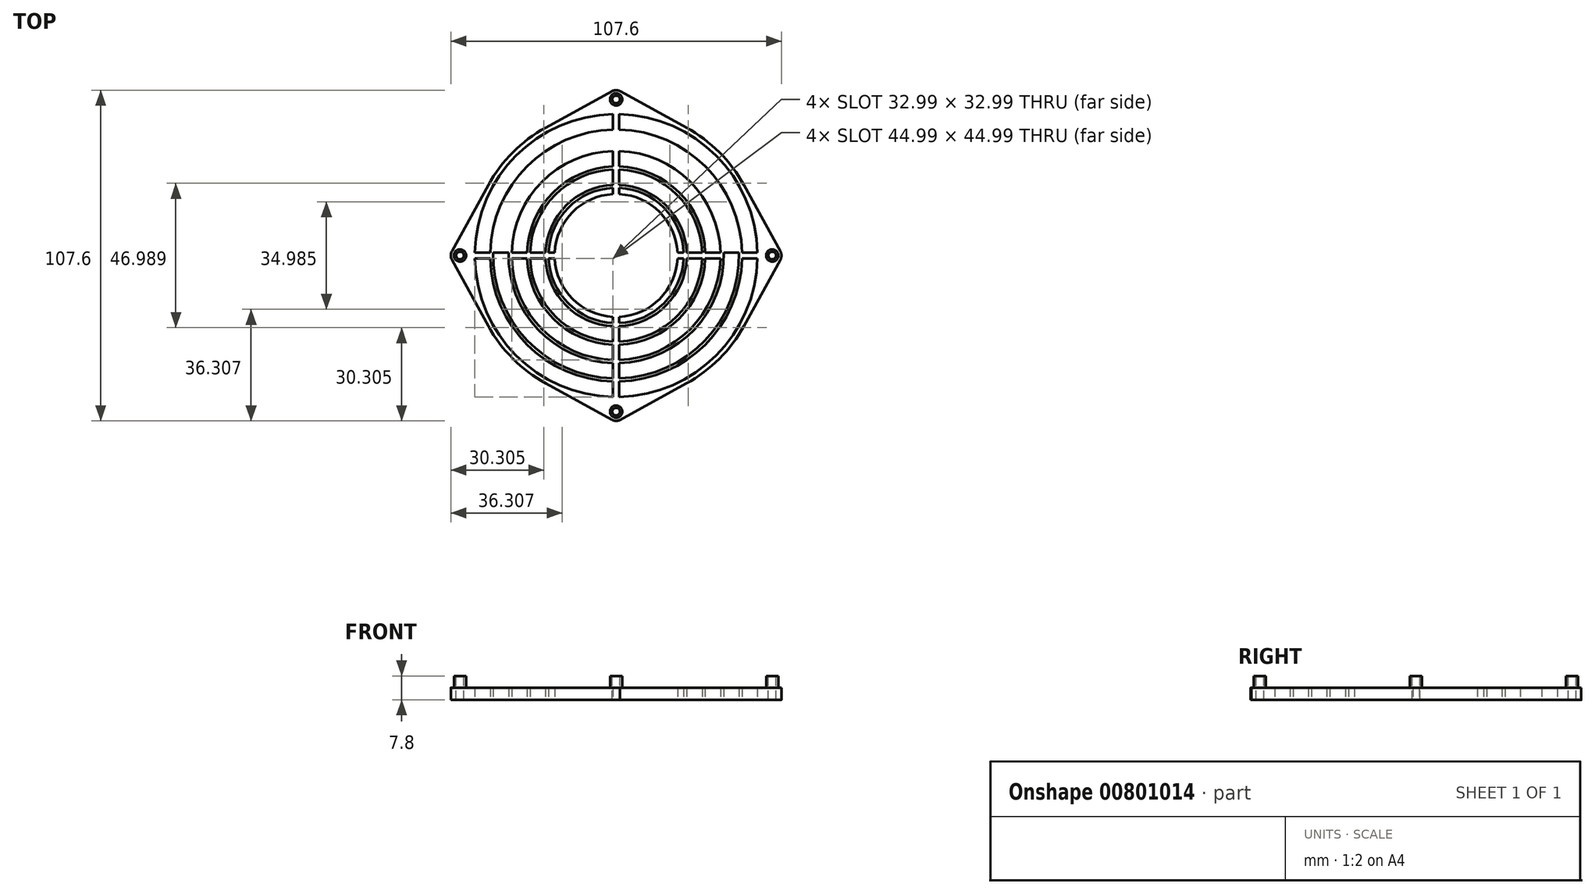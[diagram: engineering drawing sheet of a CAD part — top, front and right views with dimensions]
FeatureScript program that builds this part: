
annotation { "Feature Type Name" : "Feature", "Feature Type Description" : "" }
export const myFeature = defineFeature(function(context is Context, id is Id, definition is map)
    precondition{}
    {
        {
            var Q0;
            Q0=qCreatedBy(makeId("Top.planeOp"),FACE);
            var sketch = newSketch(context, id + "F0", { "sketchPlane" : qUnion([Q0])});
            skCircle(sketch, "E0", {"center": v(0, 0) * mm, "radius": 47.5 * mm});
            skCircle(sketch, "E1", {"center": v(0, 0) * mm, "radius": 46 * mm});
            skCircle(sketch, "E2", {"center": v(0, 0) * mm, "radius": 41 * mm});
            skCircle(sketch, "E3", {"center": v(0, 0) * mm, "radius": 40 * mm});
            skCircle(sketch, "E4", {"center": v(0, 0) * mm, "radius": 35 * mm});
            skCircle(sketch, "E5", {"center": v(0, 0) * mm, "radius": 34 * mm});
            skCircle(sketch, "E6", {"center": v(0, 0) * mm, "radius": 29 * mm});
            skCircle(sketch, "E7", {"center": v(0, 0) * mm, "radius": 28 * mm});
            skCircle(sketch, "E8", {"center": v(0, 0) * mm, "radius": 23 * mm});
            skCircle(sketch, "E9", {"center": v(0, 0) * mm, "radius": 22 * mm});
            skCircle(sketch, "E10", {"center": v(0, 0) * mm, "radius": 20 * mm});
            skLineSegment(sketch, "E11.bottom", {"start": v(-1, 47.49) * mm, "end": v(1, 47.49) * mm});
            skLineSegment(sketch, "E11.top", {"start": v(-1, -47.49) * mm, "end": v(1, -47.49) * mm});
            skLineSegment(sketch, "E11.left", {"start": v(-1, 47.49) * mm, "end": v(-1, -47.49) * mm});
            skLineSegment(sketch, "E11.right", {"start": v(1, 47.49) * mm, "end": v(1, -47.49) * mm});
            skLineSegment(sketch, "E12.bottom", {"start": v(-47.49, 1) * mm, "end": v(47.49, 1) * mm});
            skLineSegment(sketch, "E12.top", {"start": v(-47.49, -1) * mm, "end": v(47.49, -1) * mm});
            skLineSegment(sketch, "E12.left", {"start": v(-47.49, 1) * mm, "end": v(-47.49, -1) * mm});
            skLineSegment(sketch, "E12.right", {"start": v(47.49, 1) * mm, "end": v(47.49, -1) * mm});
            skCircle(sketch, "E13", {"center": v(0, 0) * mm, "radius": 50.8 * mm});
            skLineSegment(sketch, "E14", {"start": v(0, 64.35) * mm, "end": v(0, -68.55) * mm, "construction": true});
            skLineSegment(sketch, "E15", {"start": v(-68.61, 0) * mm, "end": v(59.97, 0) * mm, "construction": true});
            skCircle(sketch, "E16", {"center": v(0, 50.8) * mm, "radius": 2 * mm});
            skCircle(sketch, "E17", {"center": v(50.8, 0) * mm, "radius": 2 * mm});
            skCircle(sketch, "E18", {"center": v(0, -50.8) * mm, "radius": 2 * mm});
            skCircle(sketch, "E19", {"center": v(-50.8, 0) * mm, "radius": 2 * mm});
            skCircle(sketch, "E20", {"center": v(0, 50.8) * mm, "radius": 3 * mm});
            skLineSegment(sketch, "E21", {"start": v(-22.91, 41.6) * mm, "end": v(-1.45, 53.43) * mm});
            skCircle(sketch, "E22", {"center": v(-50.8, 0) * mm, "radius": 3 * mm});
            skCircle(sketch, "E23", {"center": v(0, -50.8) * mm, "radius": 3 * mm});
            skCircle(sketch, "E24", {"center": v(50.8, 0) * mm, "radius": 3 * mm});
            skLineSegment(sketch, "E25", {"start": v(53.43, -1.45) * mm, "end": v(41.6, -22.91) * mm});
            skLineSegment(sketch, "E26", {"start": v(53.43, 1.45) * mm, "end": v(41.6, 22.91) * mm});
            skLineSegment(sketch, "E27", {"start": v(1.45, 53.43) * mm, "end": v(22.91, 41.6) * mm});
            skLineSegment(sketch, "E28", {"start": v(-1.45, -53.43) * mm, "end": v(-22.91, -41.6) * mm});
            skLineSegment(sketch, "E29", {"start": v(1.2, -53.55) * mm, "end": v(22.89, -41.62) * mm});
            skLineSegment(sketch, "E30", {"start": v(-53.43, -1.45) * mm, "end": v(-41.6, -22.91) * mm});
            skLineSegment(sketch, "E31", {"start": v(-53.43, 1.45) * mm, "end": v(-41.6, 22.91) * mm});
            skSolve(sketch);
        }
        {
            var Q0;
            {var subQ0=sQuery(id+"F0.wireOp",EDGE,"E12.bottom");var subQ1=sQuery(id+"F0.wireOp",EDGE,"E6");var subQ2=makeQuery(id+"F0.imprint","INTERSECT",VERTEX,{"disambiguationData":[OD(1.0)],"derivedFrom":[subQ1,subQ0]});Q0=makeQuery(id+"F0.imprint","IMPRINT",FACE,{"disambiguationData":[TD([[makeQuery(id+"F0.imprint","IMPRINT",EDGE,{"disambiguationData":[TD([[subQ2,-1.0]])],"derivedFrom":subQ1}),1.0]])]});}
            var Q1;
            {var subQ1=sQuery(id+"F0.wireOp",EDGE,"E0");var subQ8=makeQuery(id+"F0.imprint","INTERSECT",VERTEX,{"derivedFrom":[subQ1,sQuery(id+"F0.wireOp",EDGE,"E26")]});Q1=makeQuery(id+"F0.imprint","IMPRINT",FACE,{"disambiguationData":[TD([[makeQuery(id+"F0.imprint","IMPRINT",EDGE,{"disambiguationData":[TD([[subQ8,-1.0]])],"derivedFrom":subQ1}),1.0]])]});}
            var Q2;
            {var subQ0=sQuery(id+"F0.wireOp",EDGE,"E11.right");var subQ1=sQuery(id+"F0.wireOp",EDGE,"E9");var subQ2=makeQuery(id+"F0.imprint","INTERSECT",VERTEX,{"disambiguationData":[OD(0.0)],"derivedFrom":[subQ1,subQ0]});Q2=makeQuery(id+"F0.imprint","IMPRINT",FACE,{"disambiguationData":[TD([[makeQuery(id+"F0.imprint","IMPRINT",EDGE,{"disambiguationData":[TD([[subQ2,-1.0]])],"derivedFrom":subQ1}),1.0]])]});}
            var Q3;
            {var subQ0=sQuery(id+"F0.wireOp",EDGE,"E12.bottom");var subQ1=sQuery(id+"F0.wireOp",EDGE,"E5");var subQ2=makeQuery(id+"F0.imprint","INTERSECT",VERTEX,{"disambiguationData":[OD(1.0)],"derivedFrom":[subQ1,subQ0]});Q3=makeQuery(id+"F0.imprint","IMPRINT",FACE,{"disambiguationData":[TD([[makeQuery(id+"F0.imprint","IMPRINT",EDGE,{"disambiguationData":[TD([[subQ2,-1.0]])],"derivedFrom":subQ1}),1.0]])]});}
            var Q4;
            {var subQ0=sQuery(id+"F0.wireOp",EDGE,"E28");var subQ1=sQuery(id+"F0.wireOp",EDGE,"E13");var subQ2=makeQuery(id+"F0.imprint","INTERSECT",VERTEX,{"derivedFrom":[subQ1,subQ0]});Q4=makeQuery(id+"F0.imprint","IMPRINT",FACE,{"disambiguationData":[TD([[makeQuery(id+"F0.imprint","IMPRINT",EDGE,{"disambiguationData":[TD([[subQ2,-1.0]])],"derivedFrom":subQ1}),1.0]])]});}
            var Q5;
            {var subQ0=sQuery(id+"F0.wireOp",EDGE,"E11.right");var subQ1=sQuery(id+"F0.wireOp",EDGE,"E10");var subQ2=makeQuery(id+"F0.imprint","INTERSECT",VERTEX,{"disambiguationData":[OD(0.0)],"derivedFrom":[subQ1,subQ0]});Q5=makeQuery(id+"F0.imprint","IMPRINT",FACE,{"disambiguationData":[TD([[makeQuery(id+"F0.imprint","IMPRINT",EDGE,{"disambiguationData":[TD([[subQ2,1.0]])],"derivedFrom":subQ1}),1.0]])]});}
            var Q6;
            {var subQ0=sQuery(id+"F0.wireOp",EDGE,"E11.right");var subQ1=sQuery(id+"F0.wireOp",EDGE,"E7");var subQ2=makeQuery(id+"F0.imprint","INTERSECT",VERTEX,{"disambiguationData":[OD(0.0)],"derivedFrom":[subQ1,subQ0]});Q6=makeQuery(id+"F0.imprint","IMPRINT",FACE,{"disambiguationData":[TD([[makeQuery(id+"F0.imprint","IMPRINT",EDGE,{"disambiguationData":[TD([[subQ2,-1.0]])],"derivedFrom":subQ1}),1.0]])]});}
            var Q7;
            {var subQ0=sQuery(id+"F0.wireOp",EDGE,"E11.right");var subQ1=sQuery(id+"F0.wireOp",EDGE,"E5");var subQ2=makeQuery(id+"F0.imprint","INTERSECT",VERTEX,{"disambiguationData":[OD(0.0)],"derivedFrom":[subQ1,subQ0]});Q7=makeQuery(id+"F0.imprint","IMPRINT",FACE,{"disambiguationData":[TD([[makeQuery(id+"F0.imprint","IMPRINT",EDGE,{"disambiguationData":[TD([[subQ2,-1.0]])],"derivedFrom":subQ1}),1.0]])]});}
            var Q8;
            {var subQ0=sQuery(id+"F0.wireOp",EDGE,"E12.bottom");var subQ1=sQuery(id+"F0.wireOp",EDGE,"E7");var subQ2=makeQuery(id+"F0.imprint","INTERSECT",VERTEX,{"disambiguationData":[OD(0.0)],"derivedFrom":[subQ1,subQ0]});Q8=makeQuery(id+"F0.imprint","IMPRINT",FACE,{"disambiguationData":[TD([[makeQuery(id+"F0.imprint","IMPRINT",EDGE,{"disambiguationData":[TD([[subQ2,1.0]])],"derivedFrom":subQ1}),1.0]])]});}
            var Q9;
            {var subQ0=sQuery(id+"F0.wireOp",EDGE,"E12.bottom");var subQ1=sQuery(id+"F0.wireOp",EDGE,"E5");var subQ2=makeQuery(id+"F0.imprint","INTERSECT",VERTEX,{"disambiguationData":[OD(0.0)],"derivedFrom":[subQ1,subQ0]});Q9=makeQuery(id+"F0.imprint","IMPRINT",FACE,{"disambiguationData":[TD([[makeQuery(id+"F0.imprint","IMPRINT",EDGE,{"disambiguationData":[TD([[subQ2,1.0]])],"derivedFrom":subQ1}),1.0]])]});}
            var Q10;
            {var subQ1=sQuery(id+"F0.wireOp",EDGE,"E0");var subQ3=makeQuery(id+"F0.imprint","INTERSECT",VERTEX,{"derivedFrom":[subQ1,sQuery(id+"F0.wireOp",EDGE,"E25")]});Q10=makeQuery(id+"F0.imprint","IMPRINT",FACE,{"disambiguationData":[TD([[makeQuery(id+"F0.imprint","IMPRINT",EDGE,{"disambiguationData":[TD([[subQ3,1.0]])],"derivedFrom":subQ1}),1.0]])]});}
            var Q11;
            {var subQ0=sQuery(id+"F0.wireOp",EDGE,"E12.bottom");var subQ1=sQuery(id+"F0.wireOp",EDGE,"E3");var subQ2=makeQuery(id+"F0.imprint","INTERSECT",VERTEX,{"disambiguationData":[OD(0.0)],"derivedFrom":[subQ1,subQ0]});Q11=makeQuery(id+"F0.imprint","IMPRINT",FACE,{"disambiguationData":[TD([[makeQuery(id+"F0.imprint","IMPRINT",EDGE,{"disambiguationData":[TD([[subQ2,1.0]])],"derivedFrom":subQ1}),1.0]])]});}
            var Q12;
            {var subQ0=sQuery(id+"F0.wireOp",EDGE,"E20");var subQ4=sQuery(id+"F0.wireOp",EDGE,"E13");var subQ8=makeQuery(id+"F0.imprint","INTERSECT",VERTEX,{"disambiguationData":[OD(0.0)],"derivedFrom":[subQ4,subQ0]});Q12=makeQuery(id+"F0.imprint","IMPRINT",FACE,{"disambiguationData":[TD([[makeQuery(id+"F0.imprint","IMPRINT",EDGE,{"disambiguationData":[TD([[subQ8,-1.0]])],"derivedFrom":subQ4}),-1.0]])]});}
            var Q13;
            {var subQ0=sQuery(id+"F0.wireOp",EDGE,"E11.right");var subQ1=sQuery(id+"F0.wireOp",EDGE,"E3");var subQ2=makeQuery(id+"F0.imprint","INTERSECT",VERTEX,{"disambiguationData":[OD(0.0)],"derivedFrom":[subQ1,subQ0]});Q13=makeQuery(id+"F0.imprint","IMPRINT",FACE,{"disambiguationData":[TD([[makeQuery(id+"F0.imprint","IMPRINT",EDGE,{"disambiguationData":[TD([[subQ2,-1.0]])],"derivedFrom":subQ1}),1.0]])]});}
            var Q14;
            {var subQ0=sQuery(id+"F0.wireOp",EDGE,"E24");var subQ1=sQuery(id+"F0.wireOp",EDGE,"E13");var subQ2=makeQuery(id+"F0.imprint","INTERSECT",VERTEX,{"disambiguationData":[OD(0.0)],"derivedFrom":[subQ1,subQ0]});Q14=makeQuery(id+"F0.imprint","IMPRINT",FACE,{"disambiguationData":[TD([[makeQuery(id+"F0.imprint","IMPRINT",EDGE,{"disambiguationData":[TD([[subQ2,1.0]])],"derivedFrom":subQ1}),1.0]])]});}
            var Q15;
            {var subQ0=sQuery(id+"F0.wireOp",EDGE,"E11.right");var subQ1=sQuery(id+"F0.wireOp",EDGE,"E6");var subQ2=makeQuery(id+"F0.imprint","INTERSECT",VERTEX,{"disambiguationData":[OD(0.0)],"derivedFrom":[subQ1,subQ0]});Q15=makeQuery(id+"F0.imprint","IMPRINT",FACE,{"disambiguationData":[TD([[makeQuery(id+"F0.imprint","IMPRINT",EDGE,{"disambiguationData":[TD([[subQ2,-1.0]])],"derivedFrom":subQ1}),1.0]])]});}
            var Q16;
            {var subQ0=sQuery(id+"F0.wireOp",EDGE,"E18");var subQ1=sQuery(id+"F0.wireOp",EDGE,"E13");var subQ2=makeQuery(id+"F0.imprint","INTERSECT",VERTEX,{"disambiguationData":[OD(0.0)],"derivedFrom":[subQ1,subQ0]});Q16=makeQuery(id+"F0.imprint","IMPRINT",FACE,{"disambiguationData":[TD([[makeQuery(id+"F0.imprint","IMPRINT",EDGE,{"disambiguationData":[TD([[subQ2,-1.0]])],"derivedFrom":subQ1}),1.0]])]});}
            var Q17;
            {var subQ5=sQuery(id+"F0.wireOp",EDGE,"E0");var subQ8=makeQuery(id+"F0.imprint","INTERSECT",VERTEX,{"derivedFrom":[subQ5,sQuery(id+"F0.wireOp",EDGE,"E21")]});Q17=makeQuery(id+"F0.imprint","IMPRINT",FACE,{"disambiguationData":[TD([[makeQuery(id+"F0.imprint","IMPRINT",EDGE,{"disambiguationData":[TD([[subQ8,-1.0]])],"derivedFrom":subQ5}),1.0]])]});}
            var Q18;
            {var subQ0=sQuery(id+"F0.wireOp",EDGE,"E18");var subQ1=sQuery(id+"F0.wireOp",EDGE,"E13");var subQ2=makeQuery(id+"F0.imprint","INTERSECT",VERTEX,{"disambiguationData":[OD(0.0)],"derivedFrom":[subQ1,subQ0]});Q18=makeQuery(id+"F0.imprint","IMPRINT",FACE,{"disambiguationData":[TD([[makeQuery(id+"F0.imprint","IMPRINT",EDGE,{"disambiguationData":[TD([[subQ2,-1.0]])],"derivedFrom":subQ1}),-1.0]])]});}
            var Q19;
            {var subQ6=sQuery(id+"F0.wireOp",EDGE,"E13");var subQ10=sQuery(id+"F0.wireOp",EDGE,"E31");var subQ11=makeQuery(id+"F0.imprint","INTERSECT",VERTEX,{"derivedFrom":[subQ6,subQ10]});Q19=makeQuery(id+"F0.imprint","IMPRINT",FACE,{"disambiguationData":[TD([[makeQuery(id+"F0.imprint","IMPRINT",EDGE,{"disambiguationData":[TD([[subQ11,-1.0]])],"derivedFrom":subQ6}),1.0]])]});}
            var Q20;
            {var subQ1=sQuery(id+"F0.wireOp",EDGE,"E13");var subQ4=sQuery(id+"F0.wireOp",EDGE,"E23");var subQ7=makeQuery(id+"F0.imprint","INTERSECT",VERTEX,{"disambiguationData":[OD(0.0)],"derivedFrom":[subQ1,subQ4]});Q20=makeQuery(id+"F0.imprint","IMPRINT",FACE,{"disambiguationData":[TD([[makeQuery(id+"F0.imprint","IMPRINT",EDGE,{"disambiguationData":[TD([[subQ7,-1.0]])],"derivedFrom":subQ1}),-1.0]])]});}
            var Q21;
            {var subQ0=sQuery(id+"F0.wireOp",EDGE,"E12.bottom");var subQ1=sQuery(id+"F0.wireOp",EDGE,"E4");var subQ2=makeQuery(id+"F0.imprint","INTERSECT",VERTEX,{"disambiguationData":[OD(1.0)],"derivedFrom":[subQ1,subQ0]});Q21=makeQuery(id+"F0.imprint","IMPRINT",FACE,{"disambiguationData":[TD([[makeQuery(id+"F0.imprint","IMPRINT",EDGE,{"disambiguationData":[TD([[subQ2,-1.0]])],"derivedFrom":subQ1}),1.0]])]});}
            var Q22;
            {var subQ0=sQuery(id+"F0.wireOp",EDGE,"E22");var subQ1=sQuery(id+"F0.wireOp",EDGE,"E13");var subQ2=makeQuery(id+"F0.imprint","INTERSECT",VERTEX,{"disambiguationData":[OD(0.0)],"derivedFrom":[subQ1,subQ0]});Q22=makeQuery(id+"F0.imprint","IMPRINT",FACE,{"disambiguationData":[TD([[makeQuery(id+"F0.imprint","IMPRINT",EDGE,{"disambiguationData":[TD([[subQ2,-1.0]])],"derivedFrom":subQ1}),1.0]])]});}
            var Q23;
            {var subQ0=sQuery(id+"F0.wireOp",EDGE,"E11.right");var subQ1=sQuery(id+"F0.wireOp",EDGE,"E8");var subQ2=makeQuery(id+"F0.imprint","INTERSECT",VERTEX,{"disambiguationData":[OD(0.0)],"derivedFrom":[subQ1,subQ0]});Q23=makeQuery(id+"F0.imprint","IMPRINT",FACE,{"disambiguationData":[TD([[makeQuery(id+"F0.imprint","IMPRINT",EDGE,{"disambiguationData":[TD([[subQ2,1.0]])],"derivedFrom":subQ1}),1.0]])]});}
            var Q24;
            {var subQ0=sQuery(id+"F0.wireOp",EDGE,"E29");var subQ1=sQuery(id+"F0.wireOp",EDGE,"E13");var subQ2=makeQuery(id+"F0.imprint","INTERSECT",VERTEX,{"derivedFrom":[subQ1,subQ0]});Q24=makeQuery(id+"F0.imprint","IMPRINT",FACE,{"disambiguationData":[TD([[makeQuery(id+"F0.imprint","IMPRINT",EDGE,{"disambiguationData":[TD([[subQ2,1.0]])],"derivedFrom":subQ1}),-1.0]])]});}
            var Q25;
            {var subQ0=sQuery(id+"F0.wireOp",EDGE,"E31");var subQ1=sQuery(id+"F0.wireOp",EDGE,"E13");var subQ2=makeQuery(id+"F0.imprint","INTERSECT",VERTEX,{"derivedFrom":[subQ1,subQ0]});Q25=makeQuery(id+"F0.imprint","IMPRINT",FACE,{"disambiguationData":[TD([[makeQuery(id+"F0.imprint","IMPRINT",EDGE,{"disambiguationData":[TD([[subQ2,-1.0]])],"derivedFrom":subQ1}),-1.0]])]});}
            var Q26;
            {var subQ0=sQuery(id+"F0.wireOp",EDGE,"E12.bottom");var subQ1=sQuery(id+"F0.wireOp",EDGE,"E10");var subQ2=makeQuery(id+"F0.imprint","INTERSECT",VERTEX,{"disambiguationData":[OD(0.0)],"derivedFrom":[subQ1,subQ0]});Q26=makeQuery(id+"F0.imprint","IMPRINT",FACE,{"disambiguationData":[TD([[makeQuery(id+"F0.imprint","IMPRINT",EDGE,{"disambiguationData":[TD([[subQ2,1.0]])],"derivedFrom":subQ1}),1.0]])]});}
            var Q27;
            {var subQ0=sQuery(id+"F0.wireOp",EDGE,"E11.right");var subQ1=sQuery(id+"F0.wireOp",EDGE,"E8");var subQ2=makeQuery(id+"F0.imprint","INTERSECT",VERTEX,{"disambiguationData":[OD(0.0)],"derivedFrom":[subQ1,subQ0]});Q27=makeQuery(id+"F0.imprint","IMPRINT",FACE,{"disambiguationData":[TD([[makeQuery(id+"F0.imprint","IMPRINT",EDGE,{"disambiguationData":[TD([[subQ2,-1.0]])],"derivedFrom":subQ1}),1.0]])]});}
            var Q28;
            {var subQ0=sQuery(id+"F0.wireOp",EDGE,"E19");var subQ1=sQuery(id+"F0.wireOp",EDGE,"E13");var subQ2=makeQuery(id+"F0.imprint","INTERSECT",VERTEX,{"disambiguationData":[OD(0.0)],"derivedFrom":[subQ1,subQ0]});Q28=makeQuery(id+"F0.imprint","IMPRINT",FACE,{"disambiguationData":[TD([[makeQuery(id+"F0.imprint","IMPRINT",EDGE,{"disambiguationData":[TD([[subQ2,-1.0]])],"derivedFrom":subQ1}),-1.0]])]});}
            var Q29;
            {var subQ0=sQuery(id+"F0.wireOp",EDGE,"E27");var subQ1=sQuery(id+"F0.wireOp",EDGE,"E13");var subQ2=makeQuery(id+"F0.imprint","INTERSECT",VERTEX,{"derivedFrom":[subQ1,subQ0]});Q29=makeQuery(id+"F0.imprint","IMPRINT",FACE,{"disambiguationData":[TD([[makeQuery(id+"F0.imprint","IMPRINT",EDGE,{"disambiguationData":[TD([[subQ2,-1.0]])],"derivedFrom":subQ1}),-1.0]])]});}
            var Q30;
            {var subQ0=sQuery(id+"F0.wireOp",EDGE,"E12.bottom");var subQ1=sQuery(id+"F0.wireOp",EDGE,"E3");var subQ2=makeQuery(id+"F0.imprint","INTERSECT",VERTEX,{"disambiguationData":[OD(1.0)],"derivedFrom":[subQ1,subQ0]});Q30=makeQuery(id+"F0.imprint","IMPRINT",FACE,{"disambiguationData":[TD([[makeQuery(id+"F0.imprint","IMPRINT",EDGE,{"disambiguationData":[TD([[subQ2,-1.0]])],"derivedFrom":subQ1}),1.0]])]});}
            var Q31;
            {var subQ0=sQuery(id+"F0.wireOp",EDGE,"E20");var subQ1=sQuery(id+"F0.wireOp",EDGE,"E13");var subQ2=makeQuery(id+"F0.imprint","INTERSECT",VERTEX,{"disambiguationData":[OD(0.0)],"derivedFrom":[subQ1,subQ0]});Q31=makeQuery(id+"F0.imprint","IMPRINT",FACE,{"disambiguationData":[TD([[makeQuery(id+"F0.imprint","IMPRINT",EDGE,{"disambiguationData":[TD([[subQ2,-1.0]])],"derivedFrom":subQ1}),1.0]])]});}
            var Q32;
            {var subQ5=sQuery(id+"F0.wireOp",EDGE,"E0");var subQ6=makeQuery(id+"F0.imprint","INTERSECT",VERTEX,{"derivedFrom":[subQ5,sQuery(id+"F0.wireOp",EDGE,"E28")]});Q32=makeQuery(id+"F0.imprint","IMPRINT",FACE,{"disambiguationData":[TD([[makeQuery(id+"F0.imprint","IMPRINT",EDGE,{"disambiguationData":[TD([[subQ6,1.0]])],"derivedFrom":subQ5}),1.0]])]});}
            var Q33;
            {var subQ0=sQuery(id+"F0.wireOp",EDGE,"E17");var subQ1=sQuery(id+"F0.wireOp",EDGE,"E13");var subQ2=makeQuery(id+"F0.imprint","INTERSECT",VERTEX,{"disambiguationData":[OD(0.0)],"derivedFrom":[subQ1,subQ0]});Q33=makeQuery(id+"F0.imprint","IMPRINT",FACE,{"disambiguationData":[TD([[makeQuery(id+"F0.imprint","IMPRINT",EDGE,{"disambiguationData":[TD([[subQ2,1.0]])],"derivedFrom":subQ1}),1.0]])]});}
            var Q34;
            {var subQ0=sQuery(id+"F0.wireOp",EDGE,"E26");var subQ1=sQuery(id+"F0.wireOp",EDGE,"E13");var subQ2=makeQuery(id+"F0.imprint","INTERSECT",VERTEX,{"derivedFrom":[subQ1,subQ0]});Q34=makeQuery(id+"F0.imprint","IMPRINT",FACE,{"disambiguationData":[TD([[makeQuery(id+"F0.imprint","IMPRINT",EDGE,{"disambiguationData":[TD([[subQ2,1.0]])],"derivedFrom":subQ1}),-1.0]])]});}
            var Q35;
            {var subQ0=sQuery(id+"F0.wireOp",EDGE,"E26");var subQ1=sQuery(id+"F0.wireOp",EDGE,"E13");var subQ2=makeQuery(id+"F0.imprint","INTERSECT",VERTEX,{"derivedFrom":[subQ1,subQ0]});Q35=makeQuery(id+"F0.imprint","IMPRINT",FACE,{"disambiguationData":[TD([[makeQuery(id+"F0.imprint","IMPRINT",EDGE,{"disambiguationData":[TD([[subQ2,1.0]])],"derivedFrom":subQ1}),1.0]])]});}
            var Q36;
            {var subQ0=sQuery(id+"F0.wireOp",EDGE,"E11.right");var subQ1=sQuery(id+"F0.wireOp",EDGE,"E2");var subQ2=makeQuery(id+"F0.imprint","INTERSECT",VERTEX,{"disambiguationData":[OD(0.0)],"derivedFrom":[subQ1,subQ0]});Q36=makeQuery(id+"F0.imprint","IMPRINT",FACE,{"disambiguationData":[TD([[makeQuery(id+"F0.imprint","IMPRINT",EDGE,{"disambiguationData":[TD([[subQ2,-1.0]])],"derivedFrom":subQ1}),1.0]])]});}
            var Q37;
            {var subQ0=sQuery(id+"F0.wireOp",EDGE,"E16");var subQ1=sQuery(id+"F0.wireOp",EDGE,"E13");var subQ2=makeQuery(id+"F0.imprint","INTERSECT",VERTEX,{"disambiguationData":[OD(0.0)],"derivedFrom":[subQ1,subQ0]});Q37=makeQuery(id+"F0.imprint","IMPRINT",FACE,{"disambiguationData":[TD([[makeQuery(id+"F0.imprint","IMPRINT",EDGE,{"disambiguationData":[TD([[subQ2,-1.0]])],"derivedFrom":subQ1}),1.0]])]});}
            var Q38;
            {var subQ0=sQuery(id+"F0.wireOp",EDGE,"E12.bottom");var subQ1=sQuery(id+"F0.wireOp",EDGE,"E1");var subQ2=makeQuery(id+"F0.imprint","INTERSECT",VERTEX,{"disambiguationData":[OD(1.0)],"derivedFrom":[subQ1,subQ0]});Q38=makeQuery(id+"F0.imprint","IMPRINT",FACE,{"disambiguationData":[TD([[makeQuery(id+"F0.imprint","IMPRINT",EDGE,{"disambiguationData":[TD([[subQ2,-1.0]])],"derivedFrom":subQ1}),1.0]])]});}
            var Q39;
            {var subQ0=sQuery(id+"F0.wireOp",EDGE,"E12.bottom");var subQ1=sQuery(id+"F0.wireOp",EDGE,"E7");var subQ2=makeQuery(id+"F0.imprint","INTERSECT",VERTEX,{"disambiguationData":[OD(1.0)],"derivedFrom":[subQ1,subQ0]});Q39=makeQuery(id+"F0.imprint","IMPRINT",FACE,{"disambiguationData":[TD([[makeQuery(id+"F0.imprint","IMPRINT",EDGE,{"disambiguationData":[TD([[subQ2,-1.0]])],"derivedFrom":subQ1}),1.0]])]});}
            var Q40;
            {var subQ0=sQuery(id+"F0.wireOp",EDGE,"E11.left");var subQ1=sQuery(id+"F0.wireOp",EDGE,"E1");var subQ2=makeQuery(id+"F0.imprint","INTERSECT",VERTEX,{"disambiguationData":[OD(1.0)],"derivedFrom":[subQ1,subQ0]});Q40=makeQuery(id+"F0.imprint","IMPRINT",FACE,{"disambiguationData":[TD([[makeQuery(id+"F0.imprint","IMPRINT",EDGE,{"disambiguationData":[TD([[subQ2,-1.0]])],"derivedFrom":subQ1}),1.0]])]});}
            var Q41;
            {var subQ0=sQuery(id+"F0.wireOp",EDGE,"E22");var subQ2=sQuery(id+"F0.wireOp",EDGE,"E13");var subQ3=makeQuery(id+"F0.imprint","INTERSECT",VERTEX,{"disambiguationData":[OD(0.0)],"derivedFrom":[subQ2,subQ0]});Q41=makeQuery(id+"F0.imprint","IMPRINT",FACE,{"disambiguationData":[TD([[makeQuery(id+"F0.imprint","IMPRINT",EDGE,{"disambiguationData":[TD([[subQ3,-1.0]])],"derivedFrom":subQ2}),-1.0]])]});}
            var Q42;
            {var subQ0=sQuery(id+"F0.wireOp",EDGE,"E27");var subQ1=sQuery(id+"F0.wireOp",EDGE,"E13");var subQ2=makeQuery(id+"F0.imprint","INTERSECT",VERTEX,{"derivedFrom":[subQ1,subQ0]});Q42=makeQuery(id+"F0.imprint","IMPRINT",FACE,{"disambiguationData":[TD([[makeQuery(id+"F0.imprint","IMPRINT",EDGE,{"disambiguationData":[TD([[subQ2,-1.0]])],"derivedFrom":subQ1}),1.0]])]});}
            var Q43;
            {var subQ0=sQuery(id+"F0.wireOp",EDGE,"E11.right");var subQ1=sQuery(id+"F0.wireOp",EDGE,"E1");var subQ2=makeQuery(id+"F0.imprint","INTERSECT",VERTEX,{"disambiguationData":[OD(0.0)],"derivedFrom":[subQ1,subQ0]});Q43=makeQuery(id+"F0.imprint","IMPRINT",FACE,{"disambiguationData":[TD([[makeQuery(id+"F0.imprint","IMPRINT",EDGE,{"disambiguationData":[TD([[subQ2,-1.0]])],"derivedFrom":subQ1}),1.0]])]});}
            var Q44;
            {var subQ0=sQuery(id+"F0.wireOp",EDGE,"E12.bottom");var subQ1=sQuery(id+"F0.wireOp",EDGE,"E4");var subQ2=makeQuery(id+"F0.imprint","INTERSECT",VERTEX,{"disambiguationData":[OD(0.0)],"derivedFrom":[subQ1,subQ0]});Q44=makeQuery(id+"F0.imprint","IMPRINT",FACE,{"disambiguationData":[TD([[makeQuery(id+"F0.imprint","IMPRINT",EDGE,{"disambiguationData":[TD([[subQ2,1.0]])],"derivedFrom":subQ1}),1.0]])]});}
            var Q45;
            {var subQ0=sQuery(id+"F0.wireOp",EDGE,"E11.right");var subQ1=sQuery(id+"F0.wireOp",EDGE,"E4");var subQ2=makeQuery(id+"F0.imprint","INTERSECT",VERTEX,{"disambiguationData":[OD(0.0)],"derivedFrom":[subQ1,subQ0]});Q45=makeQuery(id+"F0.imprint","IMPRINT",FACE,{"disambiguationData":[TD([[makeQuery(id+"F0.imprint","IMPRINT",EDGE,{"disambiguationData":[TD([[subQ2,1.0]])],"derivedFrom":subQ1}),1.0]])]});}
            var Q46;
            {var subQ0=sQuery(id+"F0.wireOp",EDGE,"E11.right");var subQ1=sQuery(id+"F0.wireOp",EDGE,"E10");var subQ2=makeQuery(id+"F0.imprint","INTERSECT",VERTEX,{"disambiguationData":[OD(0.0)],"derivedFrom":[subQ1,subQ0]});Q46=makeQuery(id+"F0.imprint","IMPRINT",FACE,{"disambiguationData":[TD([[makeQuery(id+"F0.imprint","IMPRINT",EDGE,{"disambiguationData":[TD([[subQ2,-1.0]])],"derivedFrom":subQ1}),1.0]])]});}
            var Q47;
            {var subQ0=sQuery(id+"F0.wireOp",EDGE,"E12.bottom");var subQ1=sQuery(id+"F0.wireOp",EDGE,"E2");var subQ2=makeQuery(id+"F0.imprint","INTERSECT",VERTEX,{"disambiguationData":[OD(1.0)],"derivedFrom":[subQ1,subQ0]});Q47=makeQuery(id+"F0.imprint","IMPRINT",FACE,{"disambiguationData":[TD([[makeQuery(id+"F0.imprint","IMPRINT",EDGE,{"disambiguationData":[TD([[subQ2,-1.0]])],"derivedFrom":subQ1}),1.0]])]});}
            var Q48;
            {var subQ0=sQuery(id+"F0.wireOp",EDGE,"E12.bottom");var subQ1=sQuery(id+"F0.wireOp",EDGE,"E2");var subQ2=makeQuery(id+"F0.imprint","INTERSECT",VERTEX,{"disambiguationData":[OD(0.0)],"derivedFrom":[subQ1,subQ0]});Q48=makeQuery(id+"F0.imprint","IMPRINT",FACE,{"disambiguationData":[TD([[makeQuery(id+"F0.imprint","IMPRINT",EDGE,{"disambiguationData":[TD([[subQ2,1.0]])],"derivedFrom":subQ1}),1.0]])]});}
            var Q49;
            {var subQ0=sQuery(id+"F0.wireOp",EDGE,"E11.right");var subQ1=sQuery(id+"F0.wireOp",EDGE,"E2");var subQ2=makeQuery(id+"F0.imprint","INTERSECT",VERTEX,{"disambiguationData":[OD(0.0)],"derivedFrom":[subQ1,subQ0]});Q49=makeQuery(id+"F0.imprint","IMPRINT",FACE,{"disambiguationData":[TD([[makeQuery(id+"F0.imprint","IMPRINT",EDGE,{"disambiguationData":[TD([[subQ2,1.0]])],"derivedFrom":subQ1}),1.0]])]});}
            var Q50;
            {var subQ0=sQuery(id+"F0.wireOp",EDGE,"E23");var subQ1=sQuery(id+"F0.wireOp",EDGE,"E13");var subQ2=makeQuery(id+"F0.imprint","INTERSECT",VERTEX,{"disambiguationData":[OD(0.0)],"derivedFrom":[subQ1,subQ0]});Q50=makeQuery(id+"F0.imprint","IMPRINT",FACE,{"disambiguationData":[TD([[makeQuery(id+"F0.imprint","IMPRINT",EDGE,{"disambiguationData":[TD([[subQ2,-1.0]])],"derivedFrom":subQ1}),1.0]])]});}
            var Q51;
            {var subQ0=sQuery(id+"F0.wireOp",EDGE,"E11.right");var subQ1=sQuery(id+"F0.wireOp",EDGE,"E2");var subQ2=makeQuery(id+"F0.imprint","INTERSECT",VERTEX,{"disambiguationData":[OD(1.0)],"derivedFrom":[subQ1,subQ0]});Q51=makeQuery(id+"F0.imprint","IMPRINT",FACE,{"disambiguationData":[TD([[makeQuery(id+"F0.imprint","IMPRINT",EDGE,{"disambiguationData":[TD([[subQ2,-1.0]])],"derivedFrom":subQ1}),1.0]])]});}
            var Q52;
            {var subQ0=sQuery(id+"F0.wireOp",EDGE,"E11.left");var subQ1=sQuery(id+"F0.wireOp",EDGE,"E3");var subQ2=makeQuery(id+"F0.imprint","INTERSECT",VERTEX,{"disambiguationData":[OD(1.0)],"derivedFrom":[subQ1,subQ0]});Q52=makeQuery(id+"F0.imprint","IMPRINT",FACE,{"disambiguationData":[TD([[makeQuery(id+"F0.imprint","IMPRINT",EDGE,{"disambiguationData":[TD([[subQ2,-1.0]])],"derivedFrom":subQ1}),1.0]])]});}
            var Q53;
            {var subQ0=sQuery(id+"F0.wireOp",EDGE,"E12.bottom");var subQ1=sQuery(id+"F0.wireOp",EDGE,"E1");var subQ2=makeQuery(id+"F0.imprint","INTERSECT",VERTEX,{"disambiguationData":[OD(0.0)],"derivedFrom":[subQ1,subQ0]});Q53=makeQuery(id+"F0.imprint","IMPRINT",FACE,{"disambiguationData":[TD([[makeQuery(id+"F0.imprint","IMPRINT",EDGE,{"disambiguationData":[TD([[subQ2,1.0]])],"derivedFrom":subQ1}),1.0]])]});}
            var Q54;
            {var subQ0=sQuery(id+"F0.wireOp",EDGE,"E11.left");var subQ1=sQuery(id+"F0.wireOp",EDGE,"E6");var subQ2=makeQuery(id+"F0.imprint","INTERSECT",VERTEX,{"disambiguationData":[OD(0.0)],"derivedFrom":[subQ1,subQ0]});Q54=makeQuery(id+"F0.imprint","IMPRINT",FACE,{"disambiguationData":[TD([[makeQuery(id+"F0.imprint","IMPRINT",EDGE,{"disambiguationData":[TD([[subQ2,-1.0]])],"derivedFrom":subQ1}),1.0]])]});}
            var Q55;
            {var subQ0=sQuery(id+"F0.wireOp",EDGE,"E11.right");var subQ1=sQuery(id+"F0.wireOp",EDGE,"E6");var subQ2=makeQuery(id+"F0.imprint","INTERSECT",VERTEX,{"disambiguationData":[OD(0.0)],"derivedFrom":[subQ1,subQ0]});Q55=makeQuery(id+"F0.imprint","IMPRINT",FACE,{"disambiguationData":[TD([[makeQuery(id+"F0.imprint","IMPRINT",EDGE,{"disambiguationData":[TD([[subQ2,1.0]])],"derivedFrom":subQ1}),1.0]])]});}
            var Q56;
            {var subQ0=sQuery(id+"F0.wireOp",EDGE,"E12.bottom");var subQ1=sQuery(id+"F0.wireOp",EDGE,"E6");var subQ2=makeQuery(id+"F0.imprint","INTERSECT",VERTEX,{"disambiguationData":[OD(0.0)],"derivedFrom":[subQ1,subQ0]});Q56=makeQuery(id+"F0.imprint","IMPRINT",FACE,{"disambiguationData":[TD([[makeQuery(id+"F0.imprint","IMPRINT",EDGE,{"disambiguationData":[TD([[subQ2,1.0]])],"derivedFrom":subQ1}),1.0]])]});}
            var Q57;
            {var subQ0=sQuery(id+"F0.wireOp",EDGE,"E11.left");var subQ1=sQuery(id+"F0.wireOp",EDGE,"E4");var subQ2=makeQuery(id+"F0.imprint","INTERSECT",VERTEX,{"disambiguationData":[OD(0.0)],"derivedFrom":[subQ1,subQ0]});Q57=makeQuery(id+"F0.imprint","IMPRINT",FACE,{"disambiguationData":[TD([[makeQuery(id+"F0.imprint","IMPRINT",EDGE,{"disambiguationData":[TD([[subQ2,-1.0]])],"derivedFrom":subQ1}),1.0]])]});}
            var Q58;
            {var subQ0=sQuery(id+"F0.wireOp",EDGE,"E11.left");var subQ1=sQuery(id+"F0.wireOp",EDGE,"E2");var subQ2=makeQuery(id+"F0.imprint","INTERSECT",VERTEX,{"disambiguationData":[OD(0.0)],"derivedFrom":[subQ1,subQ0]});Q58=makeQuery(id+"F0.imprint","IMPRINT",FACE,{"disambiguationData":[TD([[makeQuery(id+"F0.imprint","IMPRINT",EDGE,{"disambiguationData":[TD([[subQ2,-1.0]])],"derivedFrom":subQ1}),1.0]])]});}
            var Q59;
            {var subQ5=sQuery(id+"F0.wireOp",EDGE,"E12.right");Q59=makeQuery(id+"F0.imprint","IMPRINT",FACE,{"disambiguationData":[TD([[makeQuery(id+"F0.imprint","IMPRINT",EDGE,{"derivedFrom":subQ5}),-1.0]])]});}
            var Q60;
            {var subQ0=sQuery(id+"F0.wireOp",EDGE,"E11.left");var subQ1=sQuery(id+"F0.wireOp",EDGE,"E8");var subQ2=makeQuery(id+"F0.imprint","INTERSECT",VERTEX,{"disambiguationData":[OD(1.0)],"derivedFrom":[subQ1,subQ0]});Q60=makeQuery(id+"F0.imprint","IMPRINT",FACE,{"disambiguationData":[TD([[makeQuery(id+"F0.imprint","IMPRINT",EDGE,{"disambiguationData":[TD([[subQ2,-1.0]])],"derivedFrom":subQ1}),1.0]])]});}
            var Q61;
            {var subQ0=sQuery(id+"F0.wireOp",EDGE,"E12.bottom");var subQ1=sQuery(id+"F0.wireOp",EDGE,"E9");var subQ2=makeQuery(id+"F0.imprint","INTERSECT",VERTEX,{"disambiguationData":[OD(1.0)],"derivedFrom":[subQ1,subQ0]});Q61=makeQuery(id+"F0.imprint","IMPRINT",FACE,{"disambiguationData":[TD([[makeQuery(id+"F0.imprint","IMPRINT",EDGE,{"disambiguationData":[TD([[subQ2,-1.0]])],"derivedFrom":subQ1}),1.0]])]});}
            var Q62;
            {var subQ0=sQuery(id+"F0.wireOp",EDGE,"E11.left");var subQ1=sQuery(id+"F0.wireOp",EDGE,"E5");var subQ2=makeQuery(id+"F0.imprint","INTERSECT",VERTEX,{"disambiguationData":[OD(1.0)],"derivedFrom":[subQ1,subQ0]});Q62=makeQuery(id+"F0.imprint","IMPRINT",FACE,{"disambiguationData":[TD([[makeQuery(id+"F0.imprint","IMPRINT",EDGE,{"disambiguationData":[TD([[subQ2,-1.0]])],"derivedFrom":subQ1}),1.0]])]});}
            var Q63;
            {var subQ0=sQuery(id+"F0.wireOp",EDGE,"E11.left");var subQ1=sQuery(id+"F0.wireOp",EDGE,"E10");var subQ2=makeQuery(id+"F0.imprint","INTERSECT",VERTEX,{"disambiguationData":[OD(0.0)],"derivedFrom":[subQ1,subQ0]});Q63=makeQuery(id+"F0.imprint","IMPRINT",FACE,{"disambiguationData":[TD([[makeQuery(id+"F0.imprint","IMPRINT",EDGE,{"disambiguationData":[TD([[subQ2,-1.0]])],"derivedFrom":subQ1}),1.0]])]});}
            var Q64;
            {var subQ5=sQuery(id+"F0.wireOp",EDGE,"E12.left");Q64=makeQuery(id+"F0.imprint","IMPRINT",FACE,{"disambiguationData":[TD([[makeQuery(id+"F0.imprint","IMPRINT",EDGE,{"derivedFrom":subQ5}),1.0]])]});}
            var Q65;
            {var subQ5=sQuery(id+"F0.wireOp",EDGE,"E11.bottom");Q65=makeQuery(id+"F0.imprint","IMPRINT",FACE,{"disambiguationData":[TD([[makeQuery(id+"F0.imprint","IMPRINT",EDGE,{"derivedFrom":subQ5}),-1.0]])]});}
            var Q66;
            {var subQ0=sQuery(id+"F0.wireOp",EDGE,"E30");var subQ1=sQuery(id+"F0.wireOp",EDGE,"E13");var subQ2=makeQuery(id+"F0.imprint","INTERSECT",VERTEX,{"derivedFrom":[subQ1,subQ0]});Q66=makeQuery(id+"F0.imprint","IMPRINT",FACE,{"disambiguationData":[TD([[makeQuery(id+"F0.imprint","IMPRINT",EDGE,{"disambiguationData":[TD([[subQ2,1.0]])],"derivedFrom":subQ1}),-1.0]])]});}
            var Q67;
            {var subQ0=sQuery(id+"F0.wireOp",EDGE,"E11.right");var subQ1=sQuery(id+"F0.wireOp",EDGE,"E10");var subQ2=makeQuery(id+"F0.imprint","INTERSECT",VERTEX,{"disambiguationData":[OD(1.0)],"derivedFrom":[subQ1,subQ0]});Q67=makeQuery(id+"F0.imprint","IMPRINT",FACE,{"disambiguationData":[TD([[makeQuery(id+"F0.imprint","IMPRINT",EDGE,{"disambiguationData":[TD([[subQ2,-1.0]])],"derivedFrom":subQ1}),1.0]])]});}
            var Q68;
            {var subQ0=sQuery(id+"F0.wireOp",EDGE,"E28");var subQ1=sQuery(id+"F0.wireOp",EDGE,"E13");var subQ2=makeQuery(id+"F0.imprint","INTERSECT",VERTEX,{"derivedFrom":[subQ1,subQ0]});Q68=makeQuery(id+"F0.imprint","IMPRINT",FACE,{"disambiguationData":[TD([[makeQuery(id+"F0.imprint","IMPRINT",EDGE,{"disambiguationData":[TD([[subQ2,-1.0]])],"derivedFrom":subQ1}),-1.0]])]});}
            var Q69;
            {var subQ5=sQuery(id+"F0.wireOp",EDGE,"E11.top");Q69=makeQuery(id+"F0.imprint","IMPRINT",FACE,{"disambiguationData":[TD([[makeQuery(id+"F0.imprint","IMPRINT",EDGE,{"derivedFrom":subQ5}),1.0]])]});}
            var Q70;
            {var subQ0=sQuery(id+"F0.wireOp",EDGE,"E24");var subQ2=sQuery(id+"F0.wireOp",EDGE,"E13");var subQ3=makeQuery(id+"F0.imprint","INTERSECT",VERTEX,{"disambiguationData":[OD(0.0)],"derivedFrom":[subQ2,subQ0]});Q70=makeQuery(id+"F0.imprint","IMPRINT",FACE,{"disambiguationData":[TD([[makeQuery(id+"F0.imprint","IMPRINT",EDGE,{"disambiguationData":[TD([[subQ3,1.0]])],"derivedFrom":subQ2}),-1.0]])]});}
            var Q71;
            {var subQ0=sQuery(id+"F0.wireOp",EDGE,"E12.bottom");var subQ1=sQuery(id+"F0.wireOp",EDGE,"E9");var subQ2=makeQuery(id+"F0.imprint","INTERSECT",VERTEX,{"disambiguationData":[OD(0.0)],"derivedFrom":[subQ1,subQ0]});Q71=makeQuery(id+"F0.imprint","IMPRINT",FACE,{"disambiguationData":[TD([[makeQuery(id+"F0.imprint","IMPRINT",EDGE,{"disambiguationData":[TD([[subQ2,1.0]])],"derivedFrom":subQ1}),1.0]])]});}
            var Q72;
            {var subQ0=sQuery(id+"F0.wireOp",EDGE,"E12.bottom");var subQ1=sQuery(id+"F0.wireOp",EDGE,"E10");var subQ2=makeQuery(id+"F0.imprint","INTERSECT",VERTEX,{"disambiguationData":[OD(1.0)],"derivedFrom":[subQ1,subQ0]});Q72=makeQuery(id+"F0.imprint","IMPRINT",FACE,{"disambiguationData":[TD([[makeQuery(id+"F0.imprint","IMPRINT",EDGE,{"disambiguationData":[TD([[subQ2,-1.0]])],"derivedFrom":subQ1}),1.0]])]});}
            var Q73;
            {var subQ0=sQuery(id+"F0.wireOp",EDGE,"E11.left");var subQ1=sQuery(id+"F0.wireOp",EDGE,"E8");var subQ2=makeQuery(id+"F0.imprint","INTERSECT",VERTEX,{"disambiguationData":[OD(0.0)],"derivedFrom":[subQ1,subQ0]});Q73=makeQuery(id+"F0.imprint","IMPRINT",FACE,{"disambiguationData":[TD([[makeQuery(id+"F0.imprint","IMPRINT",EDGE,{"disambiguationData":[TD([[subQ2,-1.0]])],"derivedFrom":subQ1}),1.0]])]});}
            var Q74;
            {var subQ0=sQuery(id+"F0.wireOp",EDGE,"E11.right");var subQ1=sQuery(id+"F0.wireOp",EDGE,"E4");var subQ2=makeQuery(id+"F0.imprint","INTERSECT",VERTEX,{"disambiguationData":[OD(1.0)],"derivedFrom":[subQ1,subQ0]});Q74=makeQuery(id+"F0.imprint","IMPRINT",FACE,{"disambiguationData":[TD([[makeQuery(id+"F0.imprint","IMPRINT",EDGE,{"disambiguationData":[TD([[subQ2,-1.0]])],"derivedFrom":subQ1}),1.0]])]});}
            var Q75;
            {var subQ0=sQuery(id+"F0.wireOp",EDGE,"E12.top");var subQ1=sQuery(id+"F0.wireOp",EDGE,"E2");var subQ2=makeQuery(id+"F0.imprint","INTERSECT",VERTEX,{"disambiguationData":[OD(0.0)],"derivedFrom":[subQ1,subQ0]});Q75=makeQuery(id+"F0.imprint","IMPRINT",FACE,{"disambiguationData":[TD([[makeQuery(id+"F0.imprint","IMPRINT",EDGE,{"disambiguationData":[TD([[subQ2,-1.0]])],"derivedFrom":subQ1}),1.0]])]});}
            var Q76;
            {var subQ0=sQuery(id+"F0.wireOp",EDGE,"E12.bottom");var subQ1=sQuery(id+"F0.wireOp",EDGE,"E8");var subQ2=makeQuery(id+"F0.imprint","INTERSECT",VERTEX,{"disambiguationData":[OD(1.0)],"derivedFrom":[subQ1,subQ0]});Q76=makeQuery(id+"F0.imprint","IMPRINT",FACE,{"disambiguationData":[TD([[makeQuery(id+"F0.imprint","IMPRINT",EDGE,{"disambiguationData":[TD([[subQ2,-1.0]])],"derivedFrom":subQ1}),1.0]])]});}
            var Q77;
            {var subQ0=sQuery(id+"F0.wireOp",EDGE,"E16");var subQ1=sQuery(id+"F0.wireOp",EDGE,"E13");var subQ2=makeQuery(id+"F0.imprint","INTERSECT",VERTEX,{"disambiguationData":[OD(0.0)],"derivedFrom":[subQ1,subQ0]});Q77=makeQuery(id+"F0.imprint","IMPRINT",FACE,{"disambiguationData":[TD([[makeQuery(id+"F0.imprint","IMPRINT",EDGE,{"disambiguationData":[TD([[subQ2,-1.0]])],"derivedFrom":subQ1}),-1.0]])]});}
            var Q78;
            {var subQ0=sQuery(id+"F0.wireOp",EDGE,"E19");var subQ1=sQuery(id+"F0.wireOp",EDGE,"E13");var subQ2=makeQuery(id+"F0.imprint","INTERSECT",VERTEX,{"disambiguationData":[OD(0.0)],"derivedFrom":[subQ1,subQ0]});Q78=makeQuery(id+"F0.imprint","IMPRINT",FACE,{"disambiguationData":[TD([[makeQuery(id+"F0.imprint","IMPRINT",EDGE,{"disambiguationData":[TD([[subQ2,-1.0]])],"derivedFrom":subQ1}),1.0]])]});}
            var Q79;
            {var subQ0=sQuery(id+"F0.wireOp",EDGE,"E21");var subQ1=sQuery(id+"F0.wireOp",EDGE,"E13");var subQ2=makeQuery(id+"F0.imprint","INTERSECT",VERTEX,{"derivedFrom":[subQ1,subQ0]});Q79=makeQuery(id+"F0.imprint","IMPRINT",FACE,{"disambiguationData":[TD([[makeQuery(id+"F0.imprint","IMPRINT",EDGE,{"disambiguationData":[TD([[subQ2,1.0]])],"derivedFrom":subQ1}),-1.0]])]});}
            var Q80;
            {var subQ0=sQuery(id+"F0.wireOp",EDGE,"E11.left");var subQ1=sQuery(id+"F0.wireOp",EDGE,"E2");var subQ2=makeQuery(id+"F0.imprint","INTERSECT",VERTEX,{"disambiguationData":[OD(1.0)],"derivedFrom":[subQ1,subQ0]});Q80=makeQuery(id+"F0.imprint","IMPRINT",FACE,{"disambiguationData":[TD([[makeQuery(id+"F0.imprint","IMPRINT",EDGE,{"disambiguationData":[TD([[subQ2,-1.0]])],"derivedFrom":subQ1}),1.0]])]});}
            var Q81;
            {var subQ0=sQuery(id+"F0.wireOp",EDGE,"E11.left");var subQ1=sQuery(id+"F0.wireOp",EDGE,"E9");var subQ2=makeQuery(id+"F0.imprint","INTERSECT",VERTEX,{"disambiguationData":[OD(1.0)],"derivedFrom":[subQ1,subQ0]});Q81=makeQuery(id+"F0.imprint","IMPRINT",FACE,{"disambiguationData":[TD([[makeQuery(id+"F0.imprint","IMPRINT",EDGE,{"disambiguationData":[TD([[subQ2,-1.0]])],"derivedFrom":subQ1}),1.0]])]});}
            var Q82;
            {var subQ0=sQuery(id+"F0.wireOp",EDGE,"E12.top");var subQ1=sQuery(id+"F0.wireOp",EDGE,"E8");var subQ2=makeQuery(id+"F0.imprint","INTERSECT",VERTEX,{"disambiguationData":[OD(0.0)],"derivedFrom":[subQ1,subQ0]});Q82=makeQuery(id+"F0.imprint","IMPRINT",FACE,{"disambiguationData":[TD([[makeQuery(id+"F0.imprint","IMPRINT",EDGE,{"disambiguationData":[TD([[subQ2,-1.0]])],"derivedFrom":subQ1}),1.0]])]});}
            var Q83;
            {var subQ0=sQuery(id+"F0.wireOp",EDGE,"E11.left");var subQ1=sQuery(id+"F0.wireOp",EDGE,"E4");var subQ2=makeQuery(id+"F0.imprint","INTERSECT",VERTEX,{"disambiguationData":[OD(1.0)],"derivedFrom":[subQ1,subQ0]});Q83=makeQuery(id+"F0.imprint","IMPRINT",FACE,{"disambiguationData":[TD([[makeQuery(id+"F0.imprint","IMPRINT",EDGE,{"disambiguationData":[TD([[subQ2,-1.0]])],"derivedFrom":subQ1}),1.0]])]});}
            var Q84;
            {var subQ0=sQuery(id+"F0.wireOp",EDGE,"E11.left");var subQ1=sQuery(id+"F0.wireOp",EDGE,"E10");var subQ2=makeQuery(id+"F0.imprint","INTERSECT",VERTEX,{"disambiguationData":[OD(1.0)],"derivedFrom":[subQ1,subQ0]});Q84=makeQuery(id+"F0.imprint","IMPRINT",FACE,{"disambiguationData":[TD([[makeQuery(id+"F0.imprint","IMPRINT",EDGE,{"disambiguationData":[TD([[subQ2,-1.0]])],"derivedFrom":subQ1}),1.0]])]});}
            var Q85;
            {var subQ0=sQuery(id+"F0.wireOp",EDGE,"E12.bottom");var subQ1=sQuery(id+"F0.wireOp",EDGE,"E8");var subQ2=makeQuery(id+"F0.imprint","INTERSECT",VERTEX,{"disambiguationData":[OD(0.0)],"derivedFrom":[subQ1,subQ0]});Q85=makeQuery(id+"F0.imprint","IMPRINT",FACE,{"disambiguationData":[TD([[makeQuery(id+"F0.imprint","IMPRINT",EDGE,{"disambiguationData":[TD([[subQ2,1.0]])],"derivedFrom":subQ1}),1.0]])]});}
            var Q86;
            {var subQ0=sQuery(id+"F0.wireOp",EDGE,"E11.right");var subQ1=sQuery(id+"F0.wireOp",EDGE,"E6");var subQ2=makeQuery(id+"F0.imprint","INTERSECT",VERTEX,{"disambiguationData":[OD(1.0)],"derivedFrom":[subQ1,subQ0]});Q86=makeQuery(id+"F0.imprint","IMPRINT",FACE,{"disambiguationData":[TD([[makeQuery(id+"F0.imprint","IMPRINT",EDGE,{"disambiguationData":[TD([[subQ2,-1.0]])],"derivedFrom":subQ1}),1.0]])]});}
            var Q87;
            {var subQ0=sQuery(id+"F0.wireOp",EDGE,"E11.right");var subQ1=sQuery(id+"F0.wireOp",EDGE,"E4");var subQ2=makeQuery(id+"F0.imprint","INTERSECT",VERTEX,{"disambiguationData":[OD(0.0)],"derivedFrom":[subQ1,subQ0]});Q87=makeQuery(id+"F0.imprint","IMPRINT",FACE,{"disambiguationData":[TD([[makeQuery(id+"F0.imprint","IMPRINT",EDGE,{"disambiguationData":[TD([[subQ2,-1.0]])],"derivedFrom":subQ1}),1.0]])]});}
            var Q88;
            {var subQ0=sQuery(id+"F0.wireOp",EDGE,"E25");var subQ1=sQuery(id+"F0.wireOp",EDGE,"E13");var subQ2=makeQuery(id+"F0.imprint","INTERSECT",VERTEX,{"derivedFrom":[subQ1,subQ0]});Q88=makeQuery(id+"F0.imprint","IMPRINT",FACE,{"disambiguationData":[TD([[makeQuery(id+"F0.imprint","IMPRINT",EDGE,{"disambiguationData":[TD([[subQ2,-1.0]])],"derivedFrom":subQ1}),-1.0]])]});}
            var Q89;
            {var subQ0=sQuery(id+"F0.wireOp",EDGE,"E11.left");var subQ1=sQuery(id+"F0.wireOp",EDGE,"E6");var subQ2=makeQuery(id+"F0.imprint","INTERSECT",VERTEX,{"disambiguationData":[OD(1.0)],"derivedFrom":[subQ1,subQ0]});Q89=makeQuery(id+"F0.imprint","IMPRINT",FACE,{"disambiguationData":[TD([[makeQuery(id+"F0.imprint","IMPRINT",EDGE,{"disambiguationData":[TD([[subQ2,-1.0]])],"derivedFrom":subQ1}),1.0]])]});}
            var Q90;
            {var subQ0=sQuery(id+"F0.wireOp",EDGE,"E11.left");var subQ1=sQuery(id+"F0.wireOp",EDGE,"E7");var subQ2=makeQuery(id+"F0.imprint","INTERSECT",VERTEX,{"disambiguationData":[OD(1.0)],"derivedFrom":[subQ1,subQ0]});Q90=makeQuery(id+"F0.imprint","IMPRINT",FACE,{"disambiguationData":[TD([[makeQuery(id+"F0.imprint","IMPRINT",EDGE,{"disambiguationData":[TD([[subQ2,-1.0]])],"derivedFrom":subQ1}),1.0]])]});}
            var Q91;
            {var subQ0=sQuery(id+"F0.wireOp",EDGE,"E29");var subQ1=sQuery(id+"F0.wireOp",EDGE,"E23");var subQ2=makeQuery(id+"F0.imprint","INTERSECT",VERTEX,{"disambiguationData":[OD(0.0)],"derivedFrom":[subQ1,subQ0]});Q91=makeQuery(id+"F0.imprint","IMPRINT",FACE,{"disambiguationData":[TD([[makeQuery(id+"F0.imprint","IMPRINT",EDGE,{"disambiguationData":[TD([[subQ2,-1.0]])],"derivedFrom":subQ1}),1.0]])]});}
            var Q92;
            {var subQ0=sQuery(id+"F0.wireOp",EDGE,"E12.top");var subQ1=sQuery(id+"F0.wireOp",EDGE,"E6");var subQ2=makeQuery(id+"F0.imprint","INTERSECT",VERTEX,{"disambiguationData":[OD(0.0)],"derivedFrom":[subQ1,subQ0]});Q92=makeQuery(id+"F0.imprint","IMPRINT",FACE,{"disambiguationData":[TD([[makeQuery(id+"F0.imprint","IMPRINT",EDGE,{"disambiguationData":[TD([[subQ2,-1.0]])],"derivedFrom":subQ1}),1.0]])]});}
            var Q93;
            {var subQ0=sQuery(id+"F0.wireOp",EDGE,"E12.top");var subQ1=sQuery(id+"F0.wireOp",EDGE,"E4");var subQ2=makeQuery(id+"F0.imprint","INTERSECT",VERTEX,{"disambiguationData":[OD(0.0)],"derivedFrom":[subQ1,subQ0]});Q93=makeQuery(id+"F0.imprint","IMPRINT",FACE,{"disambiguationData":[TD([[makeQuery(id+"F0.imprint","IMPRINT",EDGE,{"disambiguationData":[TD([[subQ2,-1.0]])],"derivedFrom":subQ1}),1.0]])]});}
            var Q94;
            {var subQ0=sQuery(id+"F0.wireOp",EDGE,"E11.right");var subQ1=sQuery(id+"F0.wireOp",EDGE,"E8");var subQ2=makeQuery(id+"F0.imprint","INTERSECT",VERTEX,{"disambiguationData":[OD(1.0)],"derivedFrom":[subQ1,subQ0]});Q94=makeQuery(id+"F0.imprint","IMPRINT",FACE,{"disambiguationData":[TD([[makeQuery(id+"F0.imprint","IMPRINT",EDGE,{"disambiguationData":[TD([[subQ2,-1.0]])],"derivedFrom":subQ1}),1.0]])]});}
            var Q95;
            {var subQ0=sQuery(id+"F0.wireOp",EDGE,"E12.top");var subQ1=sQuery(id+"F0.wireOp",EDGE,"E10");var subQ2=makeQuery(id+"F0.imprint","INTERSECT",VERTEX,{"disambiguationData":[OD(0.0)],"derivedFrom":[subQ1,subQ0]});Q95=makeQuery(id+"F0.imprint","IMPRINT",FACE,{"disambiguationData":[TD([[makeQuery(id+"F0.imprint","IMPRINT",EDGE,{"disambiguationData":[TD([[subQ2,-1.0]])],"derivedFrom":subQ1}),1.0]])]});}
            var Q96;
            {var subQ0=sQuery(id+"F0.wireOp",EDGE,"E17");var subQ1=sQuery(id+"F0.wireOp",EDGE,"E13");var subQ2=makeQuery(id+"F0.imprint","INTERSECT",VERTEX,{"disambiguationData":[OD(0.0)],"derivedFrom":[subQ1,subQ0]});Q96=makeQuery(id+"F0.imprint","IMPRINT",FACE,{"disambiguationData":[TD([[makeQuery(id+"F0.imprint","IMPRINT",EDGE,{"disambiguationData":[TD([[subQ2,1.0]])],"derivedFrom":subQ1}),-1.0]])]});}
            var Q97;
            {var subQ0=sQuery(id+"F0.wireOp",EDGE,"E12.bottom");var subQ1=sQuery(id+"F0.wireOp",EDGE,"E11.left");var subQ2=makeQuery(id+"F0.imprint","INTERSECT",VERTEX,{"derivedFrom":[subQ1,subQ0]});Q97=makeQuery(id+"F0.imprint","IMPRINT",FACE,{"disambiguationData":[TD([[makeQuery(id+"F0.imprint","IMPRINT",EDGE,{"disambiguationData":[TD([[subQ2,-1.0]])],"derivedFrom":subQ1}),1.0]])]});}
            var Q98;
            {var subQ0=sQuery(id+"F0.wireOp",EDGE,"E12.right");Q98=makeQuery(id+"F0.imprint","IMPRINT",FACE,{"disambiguationData":[TD([[makeQuery(id+"F0.imprint","IMPRINT",EDGE,{"derivedFrom":subQ0}),1.0]])]});}
            var Q99;
            {var subQ0=sQuery(id+"F0.wireOp",EDGE,"E11.top");Q99=makeQuery(id+"F0.imprint","IMPRINT",FACE,{"disambiguationData":[TD([[makeQuery(id+"F0.imprint","IMPRINT",EDGE,{"derivedFrom":subQ0}),-1.0]])]});}
            var Q100;
            {var subQ0=sQuery(id+"F0.wireOp",EDGE,"E11.bottom");Q100=makeQuery(id+"F0.imprint","IMPRINT",FACE,{"disambiguationData":[TD([[makeQuery(id+"F0.imprint","IMPRINT",EDGE,{"derivedFrom":subQ0}),1.0]])]});}
            var Q101;
            {var subQ0=sQuery(id+"F0.wireOp",EDGE,"E12.left");Q101=makeQuery(id+"F0.imprint","IMPRINT",FACE,{"disambiguationData":[TD([[makeQuery(id+"F0.imprint","IMPRINT",EDGE,{"derivedFrom":subQ0}),-1.0]])]});}
            extrude(context, id + "F1", {"entities" : qUnion([Q0, Q1, Q2, Q3, Q4, Q5, Q6, Q7, Q8, Q9, Q10, Q11, Q12, Q13, Q14, Q15, Q16, Q17, Q18, Q19, Q20, Q21, Q22, Q23, Q24, Q25, Q26, Q27, Q28, Q29, Q30, Q31, Q32, Q33, Q34, Q35, Q36, Q37, Q38, Q39, Q40, Q41, Q42, Q43, Q44, Q45, Q46, Q47, Q48, Q49, Q50, Q51, Q52, Q53, Q54, Q55, Q56, Q57, Q58, Q59, Q60, Q61, Q62, Q63, Q64, Q65, Q66, Q67, Q68, Q69, Q70, Q71, Q72, Q73, Q74, Q75, Q76, Q77, Q78, Q79, Q80, Q81, Q82, Q83, Q84, Q85, Q86, Q87, Q88, Q89, Q90, Q91, Q92, Q93, Q94, Q95, Q96, Q97, Q98, Q99, Q100, Q101]), "depth" : 4 * mm, "offsetDistance" : 25 * mm});
        }
        {
            var Q0;
            Q0=makeQuery(id+"F1.opExtrude","CAP_FACE",FACE,{"disambiguationData":[OSD([sQuery(id+"F0.wireOp",EDGE,"E0"),sQuery(id+"F0.wireOp",EDGE,"E1"),sQuery(id+"F0.wireOp",EDGE,"E2"),sQuery(id+"F0.wireOp",EDGE,"E3"),sQuery(id+"F0.wireOp",EDGE,"E4"),sQuery(id+"F0.wireOp",EDGE,"E5"),sQuery(id+"F0.wireOp",EDGE,"E6"),sQuery(id+"F0.wireOp",EDGE,"E7"),sQuery(id+"F0.wireOp",EDGE,"E8"),sQuery(id+"F0.wireOp",EDGE,"E9"),sQuery(id+"F0.wireOp",EDGE,"E10"),sQuery(id+"F0.wireOp",EDGE,"E11.left"),sQuery(id+"F0.wireOp",EDGE,"E11.right"),sQuery(id+"F0.wireOp",EDGE,"E12.bottom"),sQuery(id+"F0.wireOp",EDGE,"E12.top"),sQuery(id+"F0.wireOp",EDGE,"E20"),sQuery(id+"F0.wireOp",EDGE,"E21"),sQuery(id+"F0.wireOp",EDGE,"E22"),sQuery(id+"F0.wireOp",EDGE,"E23"),sQuery(id+"F0.wireOp",EDGE,"E24"),sQuery(id+"F0.wireOp",EDGE,"E25"),sQuery(id+"F0.wireOp",EDGE,"E26"),sQuery(id+"F0.wireOp",EDGE,"E27"),sQuery(id+"F0.wireOp",EDGE,"E28"),sQuery(id+"F0.wireOp",EDGE,"E29"),sQuery(id+"F0.wireOp",EDGE,"E30"),sQuery(id+"F0.wireOp",EDGE,"E31")])],"isStart":false});
            var sketch = newSketch(context, id + "F2", { "sketchPlane" : qUnion([Q0])});
            skCircle(sketch, "E32", {"center": v(0, 50.8) * mm, "radius": 2 * mm});
            skCircle(sketch, "E33", {"center": v(50.8, 0) * mm, "radius": 2 * mm});
            skCircle(sketch, "E34", {"center": v(0, -50.8) * mm, "radius": 2 * mm});
            skCircle(sketch, "E35", {"center": v(-50.8, 0) * mm, "radius": 2 * mm});
            skSolve(sketch);
        }
        {
            var Q0;
            Q0=qSketchRegion(id+"F2",true);
            extrude(context, id + "F3", {"entities" : qUnion([Q0]), "operationType" : NewBodyOperationType.ADD, "depth" : 3.8 * mm, "offsetDistance" : 25 * mm});
        }
        {
            var Q0;
            Q0=makeQuery(id+"F3.opExtrude","CAP_FACE",FACE,{"disambiguationData":[OSD([sQuery(id+"F2.wireOp",EDGE,"E32")])],"isStart":false});
            var sketch = newSketch(context, id + "F4", { "sketchPlane" : qUnion([Q0])});
            skPoint(sketch, "E36", {"position": v(0, 50.8) * mm});
            skPoint(sketch, "E37", {"position": v(-50.8, 0) * mm});
            skPoint(sketch, "E38", {"position": v(50.8, 0) * mm});
            skPoint(sketch, "E39", {"position": v(0, -50.8) * mm});
            skSolve(sketch);
        }
        {
            var Q0;
            Q0=sQuery(id+"F4.wireOp",VERTEX,"E37");
            var Q1;
            Q1=sQuery(id+"F4.wireOp",VERTEX,"E39");
            var Q2;
            Q2=sQuery(id+"F4.wireOp",VERTEX,"E38");
            var Q3;
            Q3=sQuery(id+"F4.wireOp",VERTEX,"E36");
            var Q4;
            Q4=makeQuery(id+"F1.opExtrude","SWEPT_BODY",BODY,{"disambiguationData":[OSD([sQuery(id+"F0.wireOp",EDGE,"E0"),sQuery(id+"F0.wireOp",EDGE,"E1"),sQuery(id+"F0.wireOp",EDGE,"E2"),sQuery(id+"F0.wireOp",EDGE,"E3"),sQuery(id+"F0.wireOp",EDGE,"E4"),sQuery(id+"F0.wireOp",EDGE,"E5"),sQuery(id+"F0.wireOp",EDGE,"E6"),sQuery(id+"F0.wireOp",EDGE,"E7"),sQuery(id+"F0.wireOp",EDGE,"E8"),sQuery(id+"F0.wireOp",EDGE,"E9"),sQuery(id+"F0.wireOp",EDGE,"E10"),sQuery(id+"F0.wireOp",EDGE,"E11.left"),sQuery(id+"F0.wireOp",EDGE,"E11.right"),sQuery(id+"F0.wireOp",EDGE,"E12.bottom"),sQuery(id+"F0.wireOp",EDGE,"E12.top"),sQuery(id+"F0.wireOp",EDGE,"E20"),sQuery(id+"F0.wireOp",EDGE,"E21"),sQuery(id+"F0.wireOp",EDGE,"E22"),sQuery(id+"F0.wireOp",EDGE,"E23"),sQuery(id+"F0.wireOp",EDGE,"E24"),sQuery(id+"F0.wireOp",EDGE,"E25"),sQuery(id+"F0.wireOp",EDGE,"E26"),sQuery(id+"F0.wireOp",EDGE,"E27"),sQuery(id+"F0.wireOp",EDGE,"E28"),sQuery(id+"F0.wireOp",EDGE,"E29"),sQuery(id+"F0.wireOp",EDGE,"E30"),sQuery(id+"F0.wireOp",EDGE,"E31")])]});
            hole(context, id + "F5", {"style" : HoleStyle.SIMPLE, "endStyle" : HoleEndStyle.THROUGH, "holeDiameter" : 2.5 * mm, "majorDiameter" : 5 * mm, "isTappedThrough" : true, "tappedDepth" : 12 * mm, "tapClearance" : 3, "locations" : qUnion([Q0, Q1, Q2, Q3]), "scope" : qUnion([Q4])});
        }
    });
